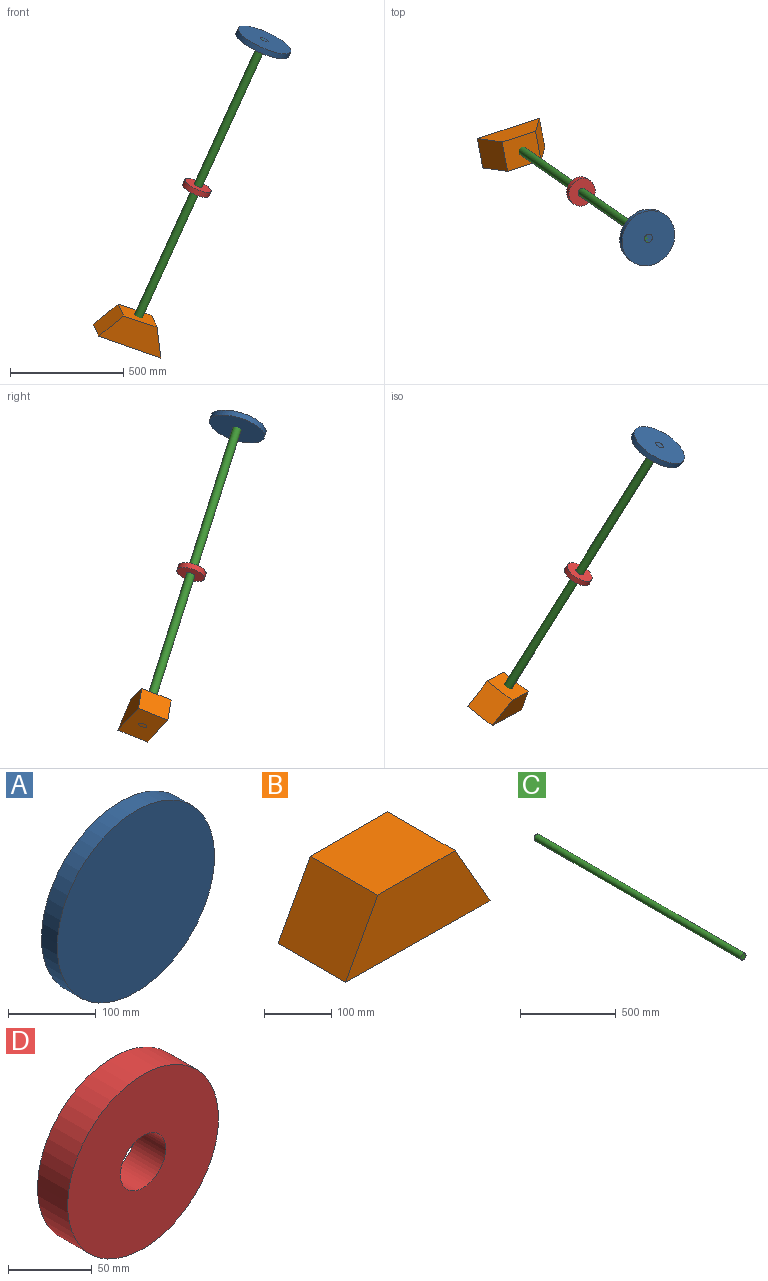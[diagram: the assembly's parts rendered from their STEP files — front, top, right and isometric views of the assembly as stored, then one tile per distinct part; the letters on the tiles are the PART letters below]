
ASSEMBLY  parts=4 mates=3
PART A: 3 faces, bbox 254x25.4x254 mm
  f0: cylinder r=127mm len=254mm, axis (0,1,0), area 20268.3mm2, adj f1,f2
  f1: plane 254x254mm, normal (0,-1,0), area 50670.7mm2, adj f0
  f2: plane 254x254mm, normal (0,1,0), area 50670.7mm2, adj f0
PART B: 6 faces, bbox 304.8x142.1x128.9 mm
  f0: plane 163.03x142.14mm, normal (0,0,1), area 23172.7mm2, adj f1,f3,f4,f5
  f1: plane 142.14x125.05mm, normal (-0.88,0,0.48), area 20238.2mm2, adj f0,f2,f4,f5
  f2: plane 304.78x142.14mm, normal (-0.01,0,-1), area 43322.7mm2, adj f1,f3,f4,f5
  f3: plane 142.14x128.87mm, normal (0.87,0,0.5), area 21096.7mm2, adj f0,f2,f4,f5
  f4: plane 304.78x128.87mm, normal (0,-1,0), area 29690.7mm2, adj f0,f1,f2,f3
  f5: plane 304.78x128.87mm, normal (0,1,0), area 29690.7mm2, adj f0,f1,f2,f3
PART C: 3 faces, bbox 38.1x1524x38.1 mm
  f0: cylinder r=19.05mm len=1524mm, axis (0,1,0), area 182414.7mm2, adj f1,f2
  f1: plane 38.1x38.1mm, normal (0,-1,0), area 1140.1mm2, adj f0
  f2: plane 38.1x38.1mm, normal (0,1,0), area 1140.1mm2, adj f0
PART D: 4 faces, bbox 127x25.4x127 mm
  f0: cylinder r=19.05mm len=38.1mm, axis (0,1,0), area 3040.2mm2, adj f2,f3
  f1: cylinder r=63.5mm len=127mm, axis (0,1,0), area 10134.1mm2, adj f2,f3
  f2: plane 127x127mm, normal (0,-1,0), area 11527.6mm2, adj f0,f1
  f3: plane 127x127mm, normal (0,1,0), area 11527.6mm2, adj f0,f1
PLACE A rot(axis=(-0.93,0.08,0.36),74.1deg) t=(-990.59,171.33,-678.94)mm
PLACE B rot(axis=(0.61,0.66,0.44),31.9deg) t=(-1622.3,598.57,-1898.75)mm
PLACE C rot(axis=(-0.93,0.08,0.36),74.1deg) t=(-1591.39,532.58,-2004.7)mm
PLACE D rot(axis=(-0.93,0.08,0.36),74.1deg) t=(-1313.11,324.35,-1325.97)mm
MATE fastened C.f0 <-> A.f0  axis (0.4,-0.28,0.87) through (-1028.3,127.25,-646.69)mm
MATE cylindrical D.f0 <-> C.f0  axis (-0.4,0.28,-0.87) through (-1332.09,338.87,-1312.71)mm
MATE fastened B.f2 <-> C.f0  axis (-0.4,0.28,-0.87) through (-1635.87,550.5,-1978.72)mm
